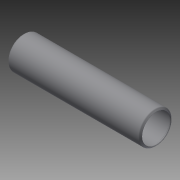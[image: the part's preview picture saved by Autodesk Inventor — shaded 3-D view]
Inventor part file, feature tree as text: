
AUTODESK INVENTOR PART (.ipt)
format: ipt  version: 2014 SP2 (Build 180246200, 246)  size: 143,360 bytes
history: native  units: in
note: dims shown in document units (in); Inventor stores cm internally (conversion verified against a paired STEP export)
features: other x42, revolve x1, sketch x1
ambient origin geometry x8: Origin, YZ Plane, XZ Plane, XY Plane, X Axis, Y Axis, Z Axis, Center Point
bodies: Solid1 (feature_tree)
feature tree (44):
  revolve  "Revolution1"  [1 undecoded]
  other  "cp1_XY"
  other  "cp1_YZ"
  other  "cp1_ZX"
  other  "cp1_X"
  other  "cp1_Y"
  other  "cp1_Z"
  other  "cp1_Center"
  other  "cp2_XY"
  other  "cp2_YZ"
  other  "cp2_ZX"
  other  "cp2_X"
  other  "cp2_Y"
  other  "cp2_Z"
  other  "cp2_Center"
  other  "cp3_XY"
  other  "cp3_YZ"
  other  "cp3_ZX"
  other  "cp3_X"
  other  "cp3_Y"
  other  "cp3_Z"
  other  "cp3_Center"
  other  "cp4_XY"
  other  "cp4_YZ"
  other  "cp4_ZX"
  other  "cp4_X"
  other  "cp4_Y"
  other  "cp4_Z"
  other  "cp4_Center"
  other  "tube_front_XY"
  other  "tube_front_YZ"
  other  "tube_front_ZX"
  other  "tube_front_X"
  other  "tube_front_Y"
  other  "tube_front_Z"
  other  "tube_front_Center"
  other  "tube_rear_XY"
  other  "tube_rear_YZ"
  other  "tube_rear_ZX"
  other  "tube_rear_X"
  other  "tube_rear_Y"
  other  "tube_rear_Z"
  other  "tube_rear_Center"
  sketch  "Sketch_1"  dims[d0=360.0deg]
note: 1 required parameter value undecoded (feature->parameter linkage not recoverable at this tier; creation-order binding heuristic only, values carry confidence <= 0.55)
